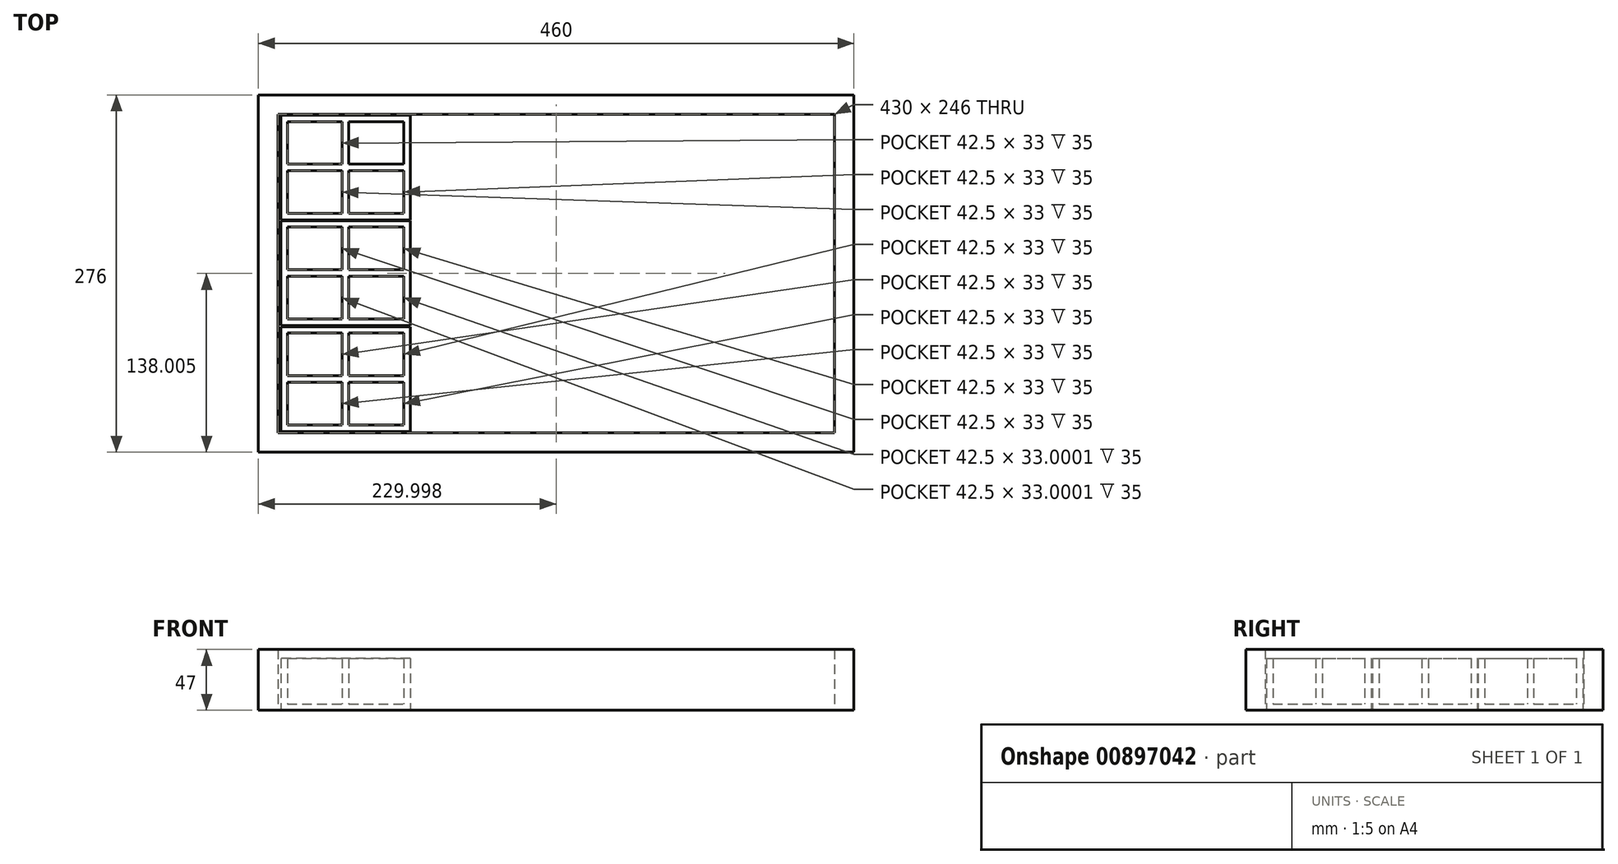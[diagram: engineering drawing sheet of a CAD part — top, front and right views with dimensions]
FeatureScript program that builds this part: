
annotation { "Feature Type Name" : "Feature", "Feature Type Description" : "" }
export const myFeature = defineFeature(function(context is Context, id is Id, definition is map)
    precondition{}
    {
        {
            var Q0;
            Q0=qCreatedBy(makeId("Top.planeOp"),FACE);
            var sketch = newSketch(context, id + "F0", { "sketchPlane" : qUnion([Q0])});
            skLineSegment(sketch, "E0.bottom", {"start": v(-229.4, -16.44) * mm, "end": v(200.6, -16.44) * mm});
            skLineSegment(sketch, "E0.top", {"start": v(-229.4, -262.44) * mm, "end": v(200.6, -262.44) * mm});
            skLineSegment(sketch, "E0.left", {"start": v(-229.4, -16.44) * mm, "end": v(-229.4, -262.44) * mm});
            skLineSegment(sketch, "E0.right", {"start": v(200.6, -16.44) * mm, "end": v(200.6, -262.44) * mm});
            skLineSegment(sketch, "E1.0", {"start": v(215.6, -1.44) * mm, "end": v(215.6, -277.44) * mm});
            skLineSegment(sketch, "E1.1", {"start": v(-244.4, -1.44) * mm, "end": v(215.6, -1.44) * mm});
            skLineSegment(sketch, "E1.2", {"start": v(-244.4, -1.44) * mm, "end": v(-244.4, -277.44) * mm});
            skLineSegment(sketch, "E1.3", {"start": v(-244.4, -277.44) * mm, "end": v(215.6, -277.44) * mm});
            skSolve(sketch);
        }
        {
            var Q0;
            Q0=makeQuery(id+"F0.imprint","IMPRINT",FACE,{"disambiguationData":[TD([[makeQuery(id+"F0.imprint","IMPRINT",EDGE,{"derivedFrom":sQuery(id+"F0.wireOp",EDGE,"E0.bottom")}),1.0]])]});
            extrude(context, id + "F1", {"entities" : qUnion([Q0]), "depth" : 47 * mm, "offsetDistance" : 25 * mm});
        }
        {
            var Q0;
            Q0=qCreatedBy(makeId("Top.planeOp"),FACE);
            var sketch = newSketch(context, id + "F2", { "sketchPlane" : qUnion([Q0])});
            skLineSegment(sketch, "E2.bottom", {"start": v(-127.13, -261.51) * mm, "end": v(-227.13, -261.51) * mm});
            skLineSegment(sketch, "E2.top", {"start": v(-127.13, -180.51) * mm, "end": v(-227.13, -180.51) * mm});
            skLineSegment(sketch, "E2.left", {"start": v(-127.13, -261.51) * mm, "end": v(-127.13, -180.51) * mm});
            skLineSegment(sketch, "E2.right", {"start": v(-227.13, -261.51) * mm, "end": v(-227.13, -180.51) * mm});
            skLineSegment(sketch, "E3.0", {"start": v(-132.13, -185.51) * mm, "end": v(-222.13, -185.51) * mm});
            skLineSegment(sketch, "E3.1", {"start": v(-132.13, -256.51) * mm, "end": v(-132.13, -185.51) * mm});
            skLineSegment(sketch, "E3.2", {"start": v(-132.13, -256.51) * mm, "end": v(-222.13, -256.51) * mm});
            skLineSegment(sketch, "E3.3", {"start": v(-222.13, -256.51) * mm, "end": v(-222.13, -185.51) * mm});
            skLineSegment(sketch, "E4.0", {"start": v(-222.13, -223.51) * mm, "end": v(-132.13, -223.51) * mm});
            skLineSegment(sketch, "E5.0", {"start": v(-222.13, -218.51) * mm, "end": v(-132.13, -218.51) * mm});
            skLineSegment(sketch, "E6.0", {"start": v(-174.63, -256.51) * mm, "end": v(-174.63, -185.51) * mm});
            skLineSegment(sketch, "E7.0", {"start": v(-179.63, -256.51) * mm, "end": v(-179.63, -185.51) * mm});
            skSolve(sketch);
        }
        {
            var Q0;
            {var subQ0=sQuery(id+"F2.wireOp",EDGE,"E4.0");var subQ1=sQuery(id+"F2.wireOp",EDGE,"E3.3");var subQ2=makeQuery(id+"F2.imprint","INTERSECT",VERTEX,{"derivedFrom":[subQ1,subQ0]});Q0=makeQuery(id+"F2.imprint","IMPRINT",FACE,{"disambiguationData":[TD([[makeQuery(id+"F2.imprint","IMPRINT",EDGE,{"disambiguationData":[TD([[subQ2,-1.0]])],"derivedFrom":subQ1}),-1.0]])]});}
            var Q1;
            {var subQ0=sQuery(id+"F2.wireOp",EDGE,"E6.0");var subQ1=sQuery(id+"F2.wireOp",EDGE,"E3.0");var subQ2=makeQuery(id+"F2.imprint","INTERSECT",VERTEX,{"derivedFrom":[subQ1,subQ0]});Q1=makeQuery(id+"F2.imprint","IMPRINT",FACE,{"disambiguationData":[TD([[makeQuery(id+"F2.imprint","IMPRINT",EDGE,{"disambiguationData":[TD([[subQ2,-1.0]])],"derivedFrom":subQ1}),1.0]])]});}
            var Q2;
            {var subQ0=sQuery(id+"F2.wireOp",EDGE,"E6.0");var subQ1=sQuery(id+"F2.wireOp",EDGE,"E3.2");var subQ2=makeQuery(id+"F2.imprint","INTERSECT",VERTEX,{"derivedFrom":[subQ1,subQ0]});Q2=makeQuery(id+"F2.imprint","IMPRINT",FACE,{"disambiguationData":[TD([[makeQuery(id+"F2.imprint","IMPRINT",EDGE,{"disambiguationData":[TD([[subQ2,-1.0]])],"derivedFrom":subQ1}),-1.0]])]});}
            var Q3;
            {var subQ0=sQuery(id+"F2.wireOp",EDGE,"E4.0");var subQ1=sQuery(id+"F2.wireOp",EDGE,"E3.1");var subQ2=makeQuery(id+"F2.imprint","INTERSECT",VERTEX,{"derivedFrom":[subQ1,subQ0]});Q3=makeQuery(id+"F2.imprint","IMPRINT",FACE,{"disambiguationData":[TD([[makeQuery(id+"F2.imprint","IMPRINT",EDGE,{"disambiguationData":[TD([[subQ2,-1.0]])],"derivedFrom":subQ1}),1.0]])]});}
            var Q4;
            {var subQ0=sQuery(id+"F2.wireOp",EDGE,"E7.0");var subQ1=sQuery(id+"F2.wireOp",EDGE,"E4.0");var subQ2=makeQuery(id+"F2.imprint","INTERSECT",VERTEX,{"derivedFrom":[subQ1,subQ0]});Q4=makeQuery(id+"F2.imprint","IMPRINT",FACE,{"disambiguationData":[TD([[makeQuery(id+"F2.imprint","IMPRINT",EDGE,{"disambiguationData":[TD([[subQ2,-1.0]])],"derivedFrom":subQ1}),1.0]])]});}
            var Q5;
            Q5=makeQuery(id+"F2.imprint","IMPRINT",FACE,{"disambiguationData":[TD([[makeQuery(id+"F2.imprint","IMPRINT",EDGE,{"derivedFrom":sQuery(id+"F2.wireOp",EDGE,"E2.bottom")}),-1.0]])]});
            extrude(context, id + "F3", {"entities" : qUnion([Q0, Q1, Q2, Q3, Q4, Q5]), "depth" : 40 * mm, "offsetDistance" : 25 * mm});
        }
        {
            var Q0;
            {var subQ0=sQuery(id+"F2.wireOp",EDGE,"E3.1");var subQ1=sQuery(id+"F2.wireOp",EDGE,"E3.0");var subQ2=makeQuery(id+"F2.imprint","INTERSECT",VERTEX,{"derivedFrom":[subQ1,subQ0]});Q0=makeQuery(id+"F2.imprint","IMPRINT",FACE,{"disambiguationData":[TD([[makeQuery(id+"F2.imprint","IMPRINT",EDGE,{"disambiguationData":[TD([[subQ2,-1.0]])],"derivedFrom":subQ1}),1.0]])]});}
            var Q1;
            {var subQ0=sQuery(id+"F2.wireOp",EDGE,"E3.2");var subQ1=sQuery(id+"F2.wireOp",EDGE,"E3.1");var subQ2=makeQuery(id+"F2.imprint","INTERSECT",VERTEX,{"derivedFrom":[subQ1,subQ0]});Q1=makeQuery(id+"F2.imprint","IMPRINT",FACE,{"disambiguationData":[TD([[makeQuery(id+"F2.imprint","IMPRINT",EDGE,{"disambiguationData":[TD([[subQ2,-1.0]])],"derivedFrom":subQ1}),1.0]])]});}
            var Q2;
            {var subQ0=sQuery(id+"F2.wireOp",EDGE,"E3.3");var subQ1=sQuery(id+"F2.wireOp",EDGE,"E3.2");var subQ2=makeQuery(id+"F2.imprint","INTERSECT",VERTEX,{"derivedFrom":[subQ1,subQ0]});Q2=makeQuery(id+"F2.imprint","IMPRINT",FACE,{"disambiguationData":[TD([[makeQuery(id+"F2.imprint","IMPRINT",EDGE,{"disambiguationData":[TD([[subQ2,1.0]])],"derivedFrom":subQ1}),-1.0]])]});}
            var Q3;
            {var subQ0=sQuery(id+"F2.wireOp",EDGE,"E3.3");var subQ1=sQuery(id+"F2.wireOp",EDGE,"E3.0");var subQ2=makeQuery(id+"F2.imprint","INTERSECT",VERTEX,{"derivedFrom":[subQ1,subQ0]});Q3=makeQuery(id+"F2.imprint","IMPRINT",FACE,{"disambiguationData":[TD([[makeQuery(id+"F2.imprint","IMPRINT",EDGE,{"disambiguationData":[TD([[subQ2,1.0]])],"derivedFrom":subQ1}),1.0]])]});}
            extrude(context, id + "F4", {"entities" : qUnion([Q0, Q1, Q2, Q3]), "operationType" : NewBodyOperationType.ADD, "depth" : 5 * mm, "offsetDistance" : 25 * mm});
        }
        {
            var Q0;
            {var subQ0=sQuery(id+"F2.wireOp",EDGE,"E3.2");var subQ1=sQuery(id+"F2.wireOp",EDGE,"E3.1");var subQ2=makeQuery(id+"F2.imprint","INTERSECT",VERTEX,{"derivedFrom":[subQ1,subQ0]});Q0=makeQuery(id+"F2.imprint","IMPRINT",FACE,{"disambiguationData":[TD([[makeQuery(id+"F2.imprint","IMPRINT",EDGE,{"disambiguationData":[TD([[subQ2,-1.0]])],"derivedFrom":subQ1}),1.0]])]});}
            var sketch = newSketch(context, id + "F5", { "sketchPlane" : qUnion([Q0])});
            skLineSegment(sketch, "E8.bottom", {"start": v(-127.1, -179.54) * mm, "end": v(-227.1, -179.54) * mm});
            skLineSegment(sketch, "E8.top", {"start": v(-127.1, -98.54) * mm, "end": v(-227.1, -98.54) * mm});
            skLineSegment(sketch, "E8.left", {"start": v(-127.1, -179.54) * mm, "end": v(-127.1, -98.54) * mm});
            skLineSegment(sketch, "E8.right", {"start": v(-227.1, -179.54) * mm, "end": v(-227.1, -98.54) * mm});
            skLineSegment(sketch, "E9.0", {"start": v(-132.1, -103.54) * mm, "end": v(-222.1, -103.54) * mm});
            skLineSegment(sketch, "E9.1", {"start": v(-132.1, -174.54) * mm, "end": v(-132.1, -103.54) * mm});
            skLineSegment(sketch, "E9.2", {"start": v(-132.1, -174.54) * mm, "end": v(-222.1, -174.54) * mm});
            skLineSegment(sketch, "E9.3", {"start": v(-222.1, -174.54) * mm, "end": v(-222.1, -103.54) * mm});
            skLineSegment(sketch, "E10.0", {"start": v(-222.1, -141.54) * mm, "end": v(-132.1, -141.54) * mm});
            skLineSegment(sketch, "E11.0", {"start": v(-222.1, -136.54) * mm, "end": v(-132.1, -136.54) * mm});
            skLineSegment(sketch, "E12.0", {"start": v(-174.6, -174.54) * mm, "end": v(-174.6, -103.54) * mm});
            skLineSegment(sketch, "E13.0", {"start": v(-179.6, -174.54) * mm, "end": v(-179.6, -103.54) * mm});
            skSolve(sketch);
        }
        {
            var Q0;
            Q0=qCreatedBy(makeId("Top.planeOp"),FACE);
            var sketch = newSketch(context, id + "F6", { "sketchPlane" : qUnion([Q0])});
            skLineSegment(sketch, "E14.bottom", {"start": v(-127.12, -98.02) * mm, "end": v(-227.12, -98.02) * mm});
            skLineSegment(sketch, "E14.top", {"start": v(-127.12, -17.02) * mm, "end": v(-227.12, -17.02) * mm});
            skLineSegment(sketch, "E14.left", {"start": v(-127.12, -98.02) * mm, "end": v(-127.12, -17.02) * mm});
            skLineSegment(sketch, "E14.right", {"start": v(-227.12, -98.02) * mm, "end": v(-227.12, -17.02) * mm});
            skLineSegment(sketch, "E15.0", {"start": v(-132.12, -22.02) * mm, "end": v(-222.12, -22.02) * mm});
            skLineSegment(sketch, "E15.1", {"start": v(-132.12, -93.02) * mm, "end": v(-132.12, -22.02) * mm});
            skLineSegment(sketch, "E15.2", {"start": v(-132.12, -93.02) * mm, "end": v(-222.12, -93.02) * mm});
            skLineSegment(sketch, "E15.3", {"start": v(-222.12, -93.02) * mm, "end": v(-222.12, -22.02) * mm});
            skLineSegment(sketch, "E16.0", {"start": v(-222.12, -60.02) * mm, "end": v(-132.12, -60.02) * mm});
            skLineSegment(sketch, "E17.0", {"start": v(-222.12, -55.02) * mm, "end": v(-132.12, -55.02) * mm});
            skLineSegment(sketch, "E18.0", {"start": v(-174.62, -93.02) * mm, "end": v(-174.62, -22.02) * mm});
            skLineSegment(sketch, "E19.0", {"start": v(-179.62, -93.02) * mm, "end": v(-179.62, -22.02) * mm});
            skSolve(sketch);
        }
        {
            var Q0;
            Q0 = qSketchRegion(id + "F5", true);
            var Q1;
            {var subQ0=sQuery(id+"F5.wireOp",EDGE,"E10.0");var subQ1=sQuery(id+"F5.wireOp",EDGE,"E9.3");var subQ2=makeQuery(id+"F5.imprint","INTERSECT",VERTEX,{"derivedFrom":[subQ1,subQ0]});Q1=makeQuery(id+"F5.imprint","IMPRINT",FACE,{"disambiguationData":[TD([[makeQuery(id+"F5.imprint","IMPRINT",EDGE,{"disambiguationData":[TD([[subQ2,-1.0]])],"derivedFrom":subQ1}),-1.0]])]});}
            var Q2;
            {var subQ0=sQuery(id+"F5.wireOp",EDGE,"E13.0");var subQ1=sQuery(id+"F5.wireOp",EDGE,"E10.0");var subQ2=makeQuery(id+"F5.imprint","INTERSECT",VERTEX,{"derivedFrom":[subQ1,subQ0]});Q2=makeQuery(id+"F5.imprint","IMPRINT",FACE,{"disambiguationData":[TD([[makeQuery(id+"F5.imprint","IMPRINT",EDGE,{"disambiguationData":[TD([[subQ2,-1.0]])],"derivedFrom":subQ1}),1.0]])]});}
            var Q3;
            {var subQ0=sQuery(id+"F5.wireOp",EDGE,"E10.0");var subQ1=sQuery(id+"F5.wireOp",EDGE,"E9.1");var subQ2=makeQuery(id+"F5.imprint","INTERSECT",VERTEX,{"derivedFrom":[subQ1,subQ0]});Q3=makeQuery(id+"F5.imprint","IMPRINT",FACE,{"disambiguationData":[TD([[makeQuery(id+"F5.imprint","IMPRINT",EDGE,{"disambiguationData":[TD([[subQ2,-1.0]])],"derivedFrom":subQ1}),1.0]])]});}
            var Q4;
            {var subQ0=sQuery(id+"F5.wireOp",EDGE,"E12.0");var subQ1=sQuery(id+"F5.wireOp",EDGE,"E9.2");var subQ2=makeQuery(id+"F5.imprint","INTERSECT",VERTEX,{"derivedFrom":[subQ1,subQ0]});Q4=makeQuery(id+"F5.imprint","IMPRINT",FACE,{"disambiguationData":[TD([[makeQuery(id+"F5.imprint","IMPRINT",EDGE,{"disambiguationData":[TD([[subQ2,-1.0]])],"derivedFrom":subQ1}),-1.0]])]});}
            var Q5;
            {var subQ0=sQuery(id+"F5.wireOp",EDGE,"E12.0");var subQ1=sQuery(id+"F5.wireOp",EDGE,"E9.0");var subQ2=makeQuery(id+"F5.imprint","INTERSECT",VERTEX,{"derivedFrom":[subQ1,subQ0]});Q5=makeQuery(id+"F5.imprint","IMPRINT",FACE,{"disambiguationData":[TD([[makeQuery(id+"F5.imprint","IMPRINT",EDGE,{"disambiguationData":[TD([[subQ2,-1.0]])],"derivedFrom":subQ1}),1.0]])]});}
            extrude(context, id + "F7", {"entities" : qUnion([Q0, Q1, Q2, Q3, Q4, Q5]), "depth" : 40 * mm, "offsetDistance" : 25 * mm});
        }
        {
            var Q0;
            {var subQ0=sQuery(id+"F5.wireOp",EDGE,"E9.3");var subQ1=sQuery(id+"F5.wireOp",EDGE,"E9.0");var subQ2=makeQuery(id+"F5.imprint","INTERSECT",VERTEX,{"derivedFrom":[subQ1,subQ0]});Q0=makeQuery(id+"F5.imprint","IMPRINT",FACE,{"disambiguationData":[TD([[makeQuery(id+"F5.imprint","IMPRINT",EDGE,{"disambiguationData":[TD([[subQ2,1.0]])],"derivedFrom":subQ1}),1.0]])]});}
            var Q1;
            {var subQ0=sQuery(id+"F5.wireOp",EDGE,"E9.3");var subQ1=sQuery(id+"F5.wireOp",EDGE,"E9.2");var subQ2=makeQuery(id+"F5.imprint","INTERSECT",VERTEX,{"derivedFrom":[subQ1,subQ0]});Q1=makeQuery(id+"F5.imprint","IMPRINT",FACE,{"disambiguationData":[TD([[makeQuery(id+"F5.imprint","IMPRINT",EDGE,{"disambiguationData":[TD([[subQ2,1.0]])],"derivedFrom":subQ1}),-1.0]])]});}
            var Q2;
            {var subQ0=sQuery(id+"F5.wireOp",EDGE,"E9.2");var subQ1=sQuery(id+"F5.wireOp",EDGE,"E9.1");var subQ2=makeQuery(id+"F5.imprint","INTERSECT",VERTEX,{"derivedFrom":[subQ1,subQ0]});Q2=makeQuery(id+"F5.imprint","IMPRINT",FACE,{"disambiguationData":[TD([[makeQuery(id+"F5.imprint","IMPRINT",EDGE,{"disambiguationData":[TD([[subQ2,-1.0]])],"derivedFrom":subQ1}),1.0]])]});}
            var Q3;
            {var subQ0=sQuery(id+"F5.wireOp",EDGE,"E9.1");var subQ1=sQuery(id+"F5.wireOp",EDGE,"E9.0");var subQ2=makeQuery(id+"F5.imprint","INTERSECT",VERTEX,{"derivedFrom":[subQ1,subQ0]});Q3=makeQuery(id+"F5.imprint","IMPRINT",FACE,{"disambiguationData":[TD([[makeQuery(id+"F5.imprint","IMPRINT",EDGE,{"disambiguationData":[TD([[subQ2,-1.0]])],"derivedFrom":subQ1}),1.0]])]});}
            extrude(context, id + "F8", {"entities" : qUnion([Q0, Q1, Q2, Q3]), "operationType" : NewBodyOperationType.ADD, "depth" : 5 * mm, "offsetDistance" : 25 * mm});
        }
        {
            var Q0;
            Q0 = qSketchRegion(id + "F6", true);
            var Q1;
            {var subQ0=sQuery(id+"F6.wireOp",EDGE,"E16.0");var subQ1=sQuery(id+"F6.wireOp",EDGE,"E15.1");var subQ2=makeQuery(id+"F6.imprint","INTERSECT",VERTEX,{"derivedFrom":[subQ1,subQ0]});Q1=makeQuery(id+"F6.imprint","IMPRINT",FACE,{"disambiguationData":[TD([[makeQuery(id+"F6.imprint","IMPRINT",EDGE,{"disambiguationData":[TD([[subQ2,-1.0]])],"derivedFrom":subQ1}),1.0]])]});}
            var Q2;
            {var subQ0=sQuery(id+"F6.wireOp",EDGE,"E19.0");var subQ1=sQuery(id+"F6.wireOp",EDGE,"E16.0");var subQ2=makeQuery(id+"F6.imprint","INTERSECT",VERTEX,{"derivedFrom":[subQ1,subQ0]});Q2=makeQuery(id+"F6.imprint","IMPRINT",FACE,{"disambiguationData":[TD([[makeQuery(id+"F6.imprint","IMPRINT",EDGE,{"disambiguationData":[TD([[subQ2,-1.0]])],"derivedFrom":subQ1}),1.0]])]});}
            var Q3;
            {var subQ0=sQuery(id+"F6.wireOp",EDGE,"E18.0");var subQ1=sQuery(id+"F6.wireOp",EDGE,"E15.0");var subQ2=makeQuery(id+"F6.imprint","INTERSECT",VERTEX,{"derivedFrom":[subQ1,subQ0]});Q3=makeQuery(id+"F6.imprint","IMPRINT",FACE,{"disambiguationData":[TD([[makeQuery(id+"F6.imprint","IMPRINT",EDGE,{"disambiguationData":[TD([[subQ2,-1.0]])],"derivedFrom":subQ1}),1.0]])]});}
            var Q4;
            {var subQ0=sQuery(id+"F6.wireOp",EDGE,"E18.0");var subQ1=sQuery(id+"F6.wireOp",EDGE,"E15.2");var subQ2=makeQuery(id+"F6.imprint","INTERSECT",VERTEX,{"derivedFrom":[subQ1,subQ0]});Q4=makeQuery(id+"F6.imprint","IMPRINT",FACE,{"disambiguationData":[TD([[makeQuery(id+"F6.imprint","IMPRINT",EDGE,{"disambiguationData":[TD([[subQ2,-1.0]])],"derivedFrom":subQ1}),-1.0]])]});}
            var Q5;
            {var subQ0=sQuery(id+"F6.wireOp",EDGE,"E16.0");var subQ1=sQuery(id+"F6.wireOp",EDGE,"E15.3");var subQ2=makeQuery(id+"F6.imprint","INTERSECT",VERTEX,{"derivedFrom":[subQ1,subQ0]});Q5=makeQuery(id+"F6.imprint","IMPRINT",FACE,{"disambiguationData":[TD([[makeQuery(id+"F6.imprint","IMPRINT",EDGE,{"disambiguationData":[TD([[subQ2,-1.0]])],"derivedFrom":subQ1}),-1.0]])]});}
            extrude(context, id + "F9", {"entities" : qUnion([Q0, Q1, Q2, Q3, Q4, Q5]), "depth" : 40 * mm, "offsetDistance" : 25 * mm});
        }
        {
            var Q0;
            {var subQ0=sQuery(id+"F6.wireOp",EDGE,"E15.2");var subQ1=sQuery(id+"F6.wireOp",EDGE,"E15.1");var subQ2=makeQuery(id+"F6.imprint","INTERSECT",VERTEX,{"derivedFrom":[subQ1,subQ0]});Q0=makeQuery(id+"F6.imprint","IMPRINT",FACE,{"disambiguationData":[TD([[makeQuery(id+"F6.imprint","IMPRINT",EDGE,{"disambiguationData":[TD([[subQ2,-1.0]])],"derivedFrom":subQ1}),1.0]])]});}
            var Q1;
            {var subQ0=sQuery(id+"F6.wireOp",EDGE,"E15.1");var subQ1=sQuery(id+"F6.wireOp",EDGE,"E15.0");var subQ2=makeQuery(id+"F6.imprint","INTERSECT",VERTEX,{"derivedFrom":[subQ1,subQ0]});Q1=makeQuery(id+"F6.imprint","IMPRINT",FACE,{"disambiguationData":[TD([[makeQuery(id+"F6.imprint","IMPRINT",EDGE,{"disambiguationData":[TD([[subQ2,-1.0]])],"derivedFrom":subQ1}),1.0]])]});}
            var Q2;
            {var subQ0=sQuery(id+"F6.wireOp",EDGE,"E15.3");var subQ1=sQuery(id+"F6.wireOp",EDGE,"E15.0");var subQ2=makeQuery(id+"F6.imprint","INTERSECT",VERTEX,{"derivedFrom":[subQ1,subQ0]});Q2=makeQuery(id+"F6.imprint","IMPRINT",FACE,{"disambiguationData":[TD([[makeQuery(id+"F6.imprint","IMPRINT",EDGE,{"disambiguationData":[TD([[subQ2,1.0]])],"derivedFrom":subQ1}),1.0]])]});}
            var Q3;
            {var subQ0=sQuery(id+"F6.wireOp",EDGE,"E15.3");var subQ1=sQuery(id+"F6.wireOp",EDGE,"E15.2");var subQ2=makeQuery(id+"F6.imprint","INTERSECT",VERTEX,{"derivedFrom":[subQ1,subQ0]});Q3=makeQuery(id+"F6.imprint","IMPRINT",FACE,{"disambiguationData":[TD([[makeQuery(id+"F6.imprint","IMPRINT",EDGE,{"disambiguationData":[TD([[subQ2,1.0]])],"derivedFrom":subQ1}),-1.0]])]});}
            extrude(context, id + "F10", {"entities" : qUnion([Q0, Q1, Q2, Q3]), "operationType" : NewBodyOperationType.ADD, "depth" : 5 * mm, "offsetDistance" : 25 * mm});
        }
    });
